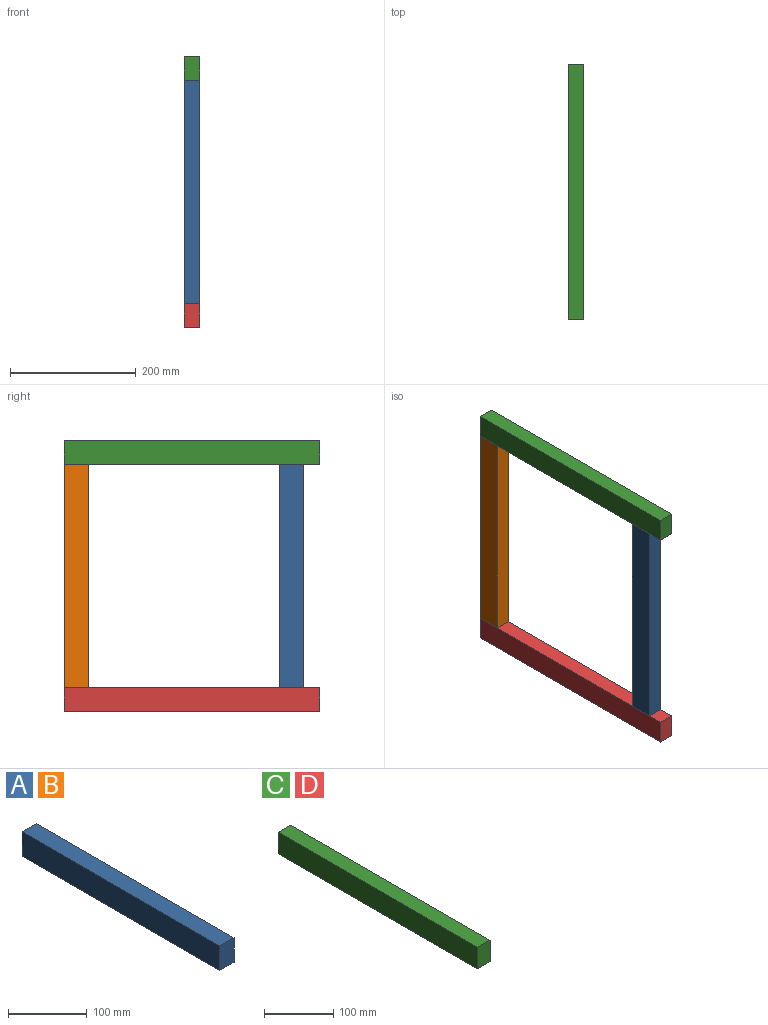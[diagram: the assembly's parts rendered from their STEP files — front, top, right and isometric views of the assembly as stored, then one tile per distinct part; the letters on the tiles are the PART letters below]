
ASSEMBLY  parts=4 mates=3
PART A: 6 faces, bbox 25.4x355.6x38.1 mm
  f0: plane 355.6x38.1mm, normal (-1,0,0), area 13548.4mm2, adj f1,f3,f4,f5
  f1: plane 355.6x25.4mm, normal (0,0,-1), area 9032.2mm2, adj f0,f2,f4,f5
  f2: plane 355.6x38.1mm, normal (1,0,0), area 13548.4mm2, adj f1,f3,f4,f5
  f3: plane 355.6x25.4mm, normal (0,0,1), area 9032.2mm2, adj f0,f2,f4,f5
  f4: plane 38.1x25.4mm, normal (0,-1,0), area 967.7mm2, adj f0,f1,f2,f3
  f5: plane 38.1x25.4mm, normal (0,1,0), area 967.7mm2, adj f0,f1,f2,f3
PART B: same geometry as A
PART C: 6 faces, bbox 25.4x406.4x38.1 mm
  f0: plane 406.4x38.1mm, normal (-1,0,0), area 15483.8mm2, adj f1,f3,f4,f5
  f1: plane 406.4x25.4mm, normal (0,0,-1), area 10322.6mm2, adj f0,f2,f4,f5
  f2: plane 406.4x38.1mm, normal (1,0,0), area 15483.8mm2, adj f1,f3,f4,f5
  f3: plane 406.4x25.4mm, normal (0,0,1), area 10322.6mm2, adj f0,f2,f4,f5
  f4: plane 38.1x25.4mm, normal (0,-1,0), area 967.7mm2, adj f0,f1,f2,f3
  f5: plane 38.1x25.4mm, normal (0,1,0), area 967.7mm2, adj f0,f1,f2,f3
PART D: same geometry as C
PLACE A rot(axis=(1,0,0),90deg) t=(0,-342.9,393.7)mm
PLACE B rot(axis=(1,0,0),90deg) t=(0,0,393.7)mm
PLACE C t=(0,0,393.7)mm
PLACE D at identity fixed
MATE fastened A.f4 <-> D.f3  axis (0,0,-1) through (25.4,-381,38.1)mm
MATE fastened A.f5 <-> C.f1  axis (0,0,1) through (25.4,-381,393.7)mm
MATE fastened B.f4 <-> D.f3  axis (0,0,-1) through (25.4,0,38.1)mm
